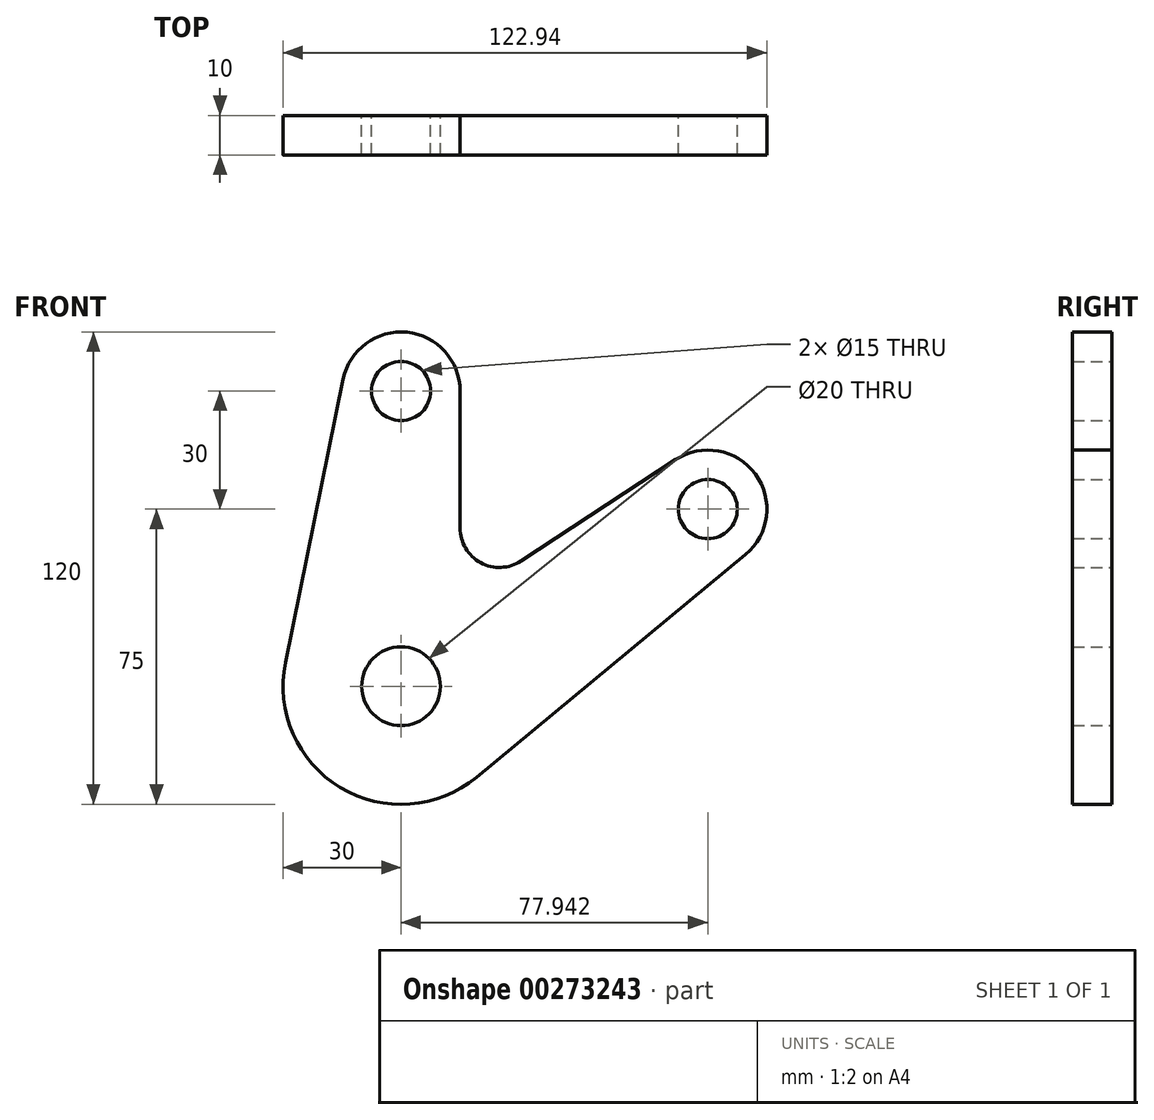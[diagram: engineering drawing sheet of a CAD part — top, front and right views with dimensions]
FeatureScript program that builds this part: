
annotation { "Feature Type Name" : "Feature", "Feature Type Description" : "" }
export const myFeature = defineFeature(function(context is Context, id is Id, definition is map)
    precondition{}
    {
        {
            var Q0;
            Q0=qCreatedBy(makeId("Front.planeOp"),FACE);
            var sketch = newSketch(context, id + "F0", { "sketchPlane" : qUnion([Q0])});
            skCircle(sketch, "E0", {"center": v(0, 0) * mm, "radius": 10 * mm});
            skLineSegment(sketch, "E1", {"start": v(0, 0) * mm, "end": v(0, 75) * mm, "construction": true});
            skLineSegment(sketch, "E2", {"start": v(0, 0) * mm, "end": v(77.94, 45) * mm, "construction": true});
            skCircle(sketch, "E3", {"center": v(0, 75) * mm, "radius": 7.5 * mm});
            skCircle(sketch, "E4", {"center": v(77.94, 45) * mm, "radius": 7.5 * mm});
            skLineSegment(sketch, "E5", {"start": v(-14.7, 78) * mm, "end": v(-29.4, 6) * mm});
            skLineSegment(sketch, "E6", {"start": v(19.12, -23.12) * mm, "end": v(87.5, 33.44) * mm});
            skLineSegment(sketch, "E7", {"start": v(15, 75) * mm, "end": v(15, 40.19) * mm});
            skArc(sketch, "E8", {"start": v(-14.7, 78) * mm, "mid": v(1.5, 89.92) * mm, "end": v(15, 75) * mm});
            skArc(sketch, "E9", {"start": v(-29.4, 6) * mm, "mid": v(-15.44, -25.72) * mm, "end": v(19.12, -23.12) * mm});
            skArc(sketch, "E10", {"start": v(87.5, 33.44) * mm, "mid": v(90.01, 53.9) * mm, "end": v(69.72, 57.55) * mm});
            skLineSegment(sketch, "E11", {"start": v(30.48, 31.83) * mm, "end": v(69.72, 57.55) * mm});
            skPoint(sketch, "E12.visualSharp", {"position": v(15, 21.68) * mm});
            skArc(sketch, "E12.filletArc", {"start": v(15, 40.19) * mm, "mid": v(20.25, 31.4) * mm, "end": v(30.48, 31.83) * mm});
            skSolve(sketch);
        }
        {
            var Q0;
            Q0 = qSketchRegion(id + "F0", true);
            extrude(context, id + "F1", {"entities" : qUnion([Q0]), "depth" : 10 * mm});
        }
    });
